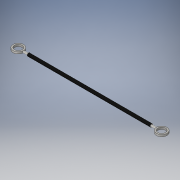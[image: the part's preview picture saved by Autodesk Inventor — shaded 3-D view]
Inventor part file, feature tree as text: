
AUTODESK INVENTOR PART (.ipt)
format: ipt  version: 2016 (Build 200138000, 138)  size: 136,704 bytes
history: native  units: in
note: dims shown in document units (in); Inventor stores cm internally (conversion verified against a paired STEP export)
features: extrude x3, sketch x3, other x2, mirror x1
ambient origin geometry x8: Origin, YZ Plane, XZ Plane, XY Plane, X Axis, Y Axis, Z Axis, Center Point
bodies: Solid1 (feature_tree)
feature tree (9):
  extrude  "Black Shaft"  Depth=0.1875in
  extrude  "Screwed Shaft"  Depth=12.5in TaperAngle=0.0deg
  other  "Mid Plane"
  extrude  "Rod End1"  Depth=0.1875in
  mirror  "Rod End2"
  other  "Horizontal Midplane"
  sketch  "Sketch1"  dims[d0=12.0in d1=0.0in d2=0.1875in]
  sketch  "Sketch3"  dims[d3=0.5in d4=0.0in d5=12.5in d6=0.0in]
  sketch  "Sketch4"  dims[d7=1.0313in d8=0.5in d9=0.75in d10=0.1875in d11=0.0in]
